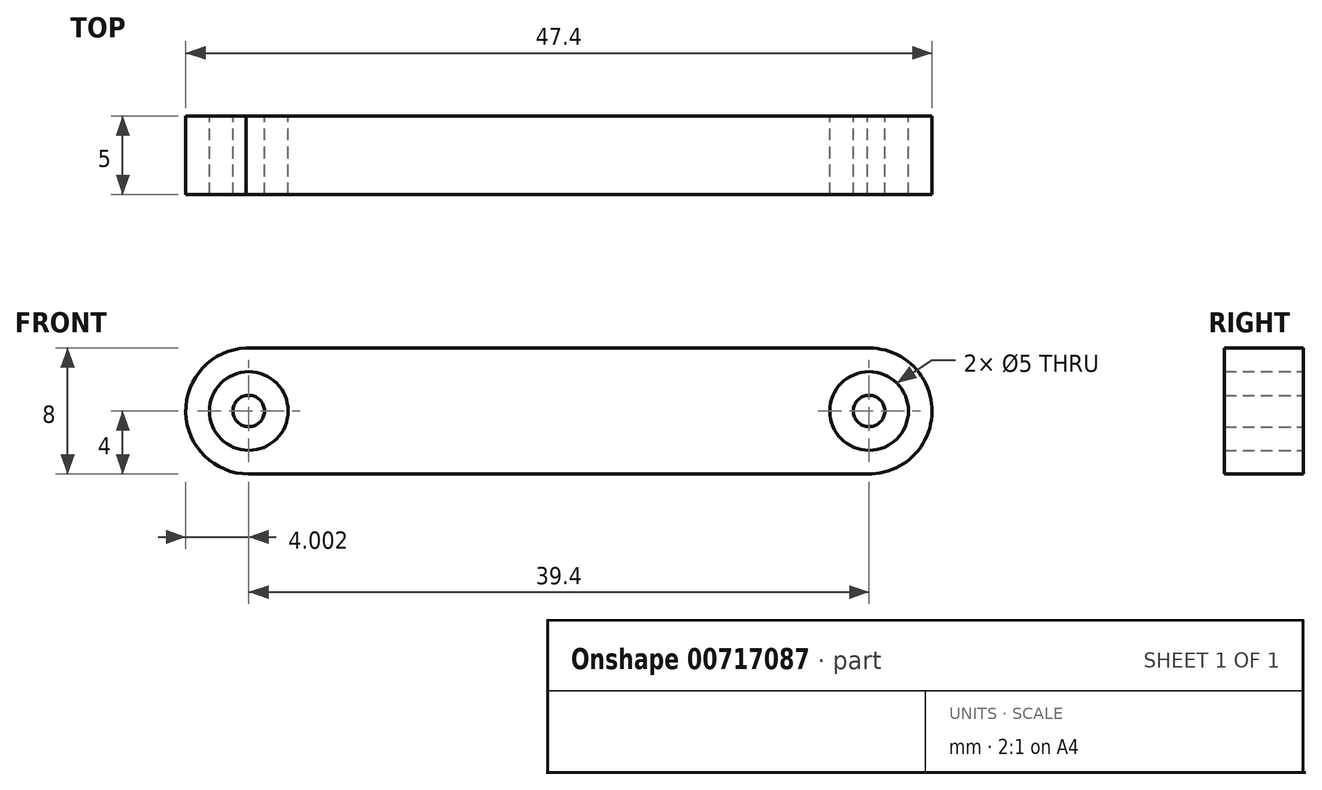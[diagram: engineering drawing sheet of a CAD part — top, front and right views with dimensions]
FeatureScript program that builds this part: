
annotation { "Feature Type Name" : "Feature", "Feature Type Description" : "" }
export const myFeature = defineFeature(function(context is Context, id is Id, definition is map)
    precondition{}
    {
        {
            var Q0;
            Q0=qCreatedBy(makeId("Front.planeOp"),FACE);
            var sketch = newSketch(context, id + "F0", { "sketchPlane" : qUnion([Q0])});
            skLineSegment(sketch, "E0", {"start": v(-15.9, 21.14) * mm, "end": v(23.5, 21.14) * mm});
            skCircle(sketch, "E1", {"center": v(-15.9, 21.14) * mm, "radius": 2.5 * mm});
            skCircle(sketch, "E2", {"center": v(-15.9, 21.14) * mm, "radius": 1 * mm});
            skArc(sketch, "E3", {"start": v(-15.74, 25.14) * mm, "mid": v(-19.9, 21.22) * mm, "end": v(-15.9, 17.14) * mm});
            skCircle(sketch, "E4", {"center": v(23.5, 21.14) * mm, "radius": 1 * mm});
            skCircle(sketch, "E5", {"center": v(23.5, 21.14) * mm, "radius": 2.5 * mm});
            skArc(sketch, "E6", {"start": v(23.4, 17.14) * mm, "mid": v(27.5, 21.09) * mm, "end": v(23.5, 25.14) * mm});
            skLineSegment(sketch, "E7", {"start": v(-16.07, 25.14) * mm, "end": v(23.5, 25.14) * mm});
            skLineSegment(sketch, "E8", {"start": v(23.4, 17.14) * mm, "end": v(-15.9, 17.14) * mm});
            skSolve(sketch);
        }
        {
            var Q0;
            Q0=makeQuery(id+"F0.imprint","IMPRINT",FACE,{"disambiguationData":[TD([[makeQuery(id+"F0.imprint","IMPRINT",EDGE,{"derivedFrom":sQuery(id+"F0.wireOp",EDGE,"E1")}),-1.0]])]});
            extrude(context, id + "F1", {"entities" : qUnion([Q0]), "depth" : 5 * mm, "offsetDistance" : 25.4 * mm});
        }
        {
            var Q0;
            Q0=makeQuery(id+"F0.imprint","IMPRINT",FACE,{"disambiguationData":[TD([[makeQuery(id+"F0.imprint","IMPRINT",EDGE,{"derivedFrom":sQuery(id+"F0.wireOp",EDGE,"E2")}),1.0]])]});
            var Q1;
            Q1=makeQuery(id+"F0.imprint","IMPRINT",FACE,{"disambiguationData":[TD([[makeQuery(id+"F0.imprint","IMPRINT",EDGE,{"derivedFrom":sQuery(id+"F0.wireOp",EDGE,"E4")}),1.0]])]});
            extrude(context, id + "F2", {"entities" : qUnion([Q0, Q1]), "depth" : 5 * mm, "offsetDistance" : 25.4 * mm});
        }
    });
